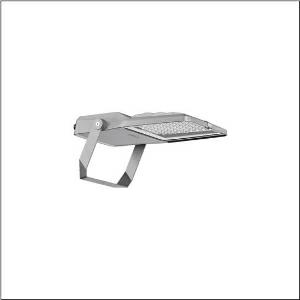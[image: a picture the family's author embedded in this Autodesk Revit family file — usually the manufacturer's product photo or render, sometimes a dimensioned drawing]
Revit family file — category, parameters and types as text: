
# Revit family: floodlight_fl_21_iq_mini___pl52_5xa7772c2d1a_8042
name_source: partatom
category: Lighting Fixtures
units: mm (PartAtom-declared; Revit-internal decimal feet)

## family parameters
Cut with Voids When Loaded = No
Host = Face
Light Source = No
Part Type = Normal
Room Calculation Point = No
Round Connector Dimension = Use Diameter
Shared = No

## types (1)
- --- (1 x LED, 12210 lm, 87.2 W, 3000K)
    Apparent Load = 87 VA
    CIE Flux Codes = 26 60 98 100 100
    Color Rendering = 70
    Color Temperature = 3000K
    Default Elevation = 1800 mm
    Description = Floodlight FL 21 iQ mini, floodlight, primary light control with lens, of PMMA, primary optical cover: protective disc, of toughened safety glass, transparent, light distribution: PL52, light emission: direct distribution, installation type: surface-mounted, LED, High Power LED, rated luminous flux: 12.210lm, luminous efficacy: 140lm/W, light colour: 730, colour temperature: 3000K, control gear: iQ Street-Remote/DALI, control: Street-Remote, Auto-Match, Temp-Guard, Night-Set, Smart-Wire, Desk-Remote (wireless, voltage-free reading and setting of iQ features in the workshop via application-optimized NFC function/RFID function), optimised constant luminous flux control (CLO 2.0), with terminal, 6-pole, mains connection: 220..240V, AC, 50/60Hz, start of lifetime: 87W, end of service life: 92W, reduction: 40W, luminaire housing, of diecast aluminium, powder-coated, Siteco® metallic grey (DB 702S), corrosivity category C5 mid according to DIN EN ISO 12944, suitable for swimming pools, chlorine-resistant, sealing non-destructively replaceable, mounting bracket, of steel, galvanised, powder-coated, Siteco® metallic grey (DB 702S), protection rating (complete): IP66, insulation class (complete): insulation class II (safety insulation), certification: CE, ENEC, VDE, protection symbol: D, impact resistance: IK08, permissible operating ambient temperature: -40..+40°C, permissible operating ambient temperature for outdoor applications: -40..+50°C, standard: DIN EN 12944, LABS conformity tested according to VDMA 24364:2018-05, packaging unit: 1 piece

Light Distribution: PL52
    Height = 70 mm
    Lamp = 1 x LED
    Lamp Light Flux = 12210 lm
    Lamp Power = 87.2 W
    Lamp count = 1
    Length = 485 mm
    Luminous efficacy = 140 lm/W
    Manufacturer = Siteco
    ModVariant = No
    Model = 5XA7772C2D1A
    Number of Poles = 1
    OnlyDefault = Yes
    Power Factor = 1
    Product Name = Floodlight FL 21 iQ mini | PL52
    Product group = floodlight | pylon annexe
    ProductGroupID = 6200
    Protection Class = Protection class II
    Protection Degree = IP 66
    RLX_Detail_Level = 1
    RLX_Emergency_Light_Flux = 0 lm
    RLX_Emergency_Type = 0
    RLX_Emergency_Type_DB = No
    RlxData = <blob elided: 96613 chars, md5=5d702614>
    Socket = socket
    Standby Power = 0 W
    System Light Flux = 12210 lm
    System Power = 87 W
    Type Comments = factory setting: luminous flux: 100 % | dim-lin: 254 | 456 mA
    Type Image = l_1006845.jpg
    URL = http://relux.com
    VarID = @adj_164376
    Voltage = 0 V
    Weight = 0.00 kg
    Width = 337 mm

## geometry (parser evidence)
native form markers: Blend x4, Sweep x10
no freeform markers — native parametric forms only
